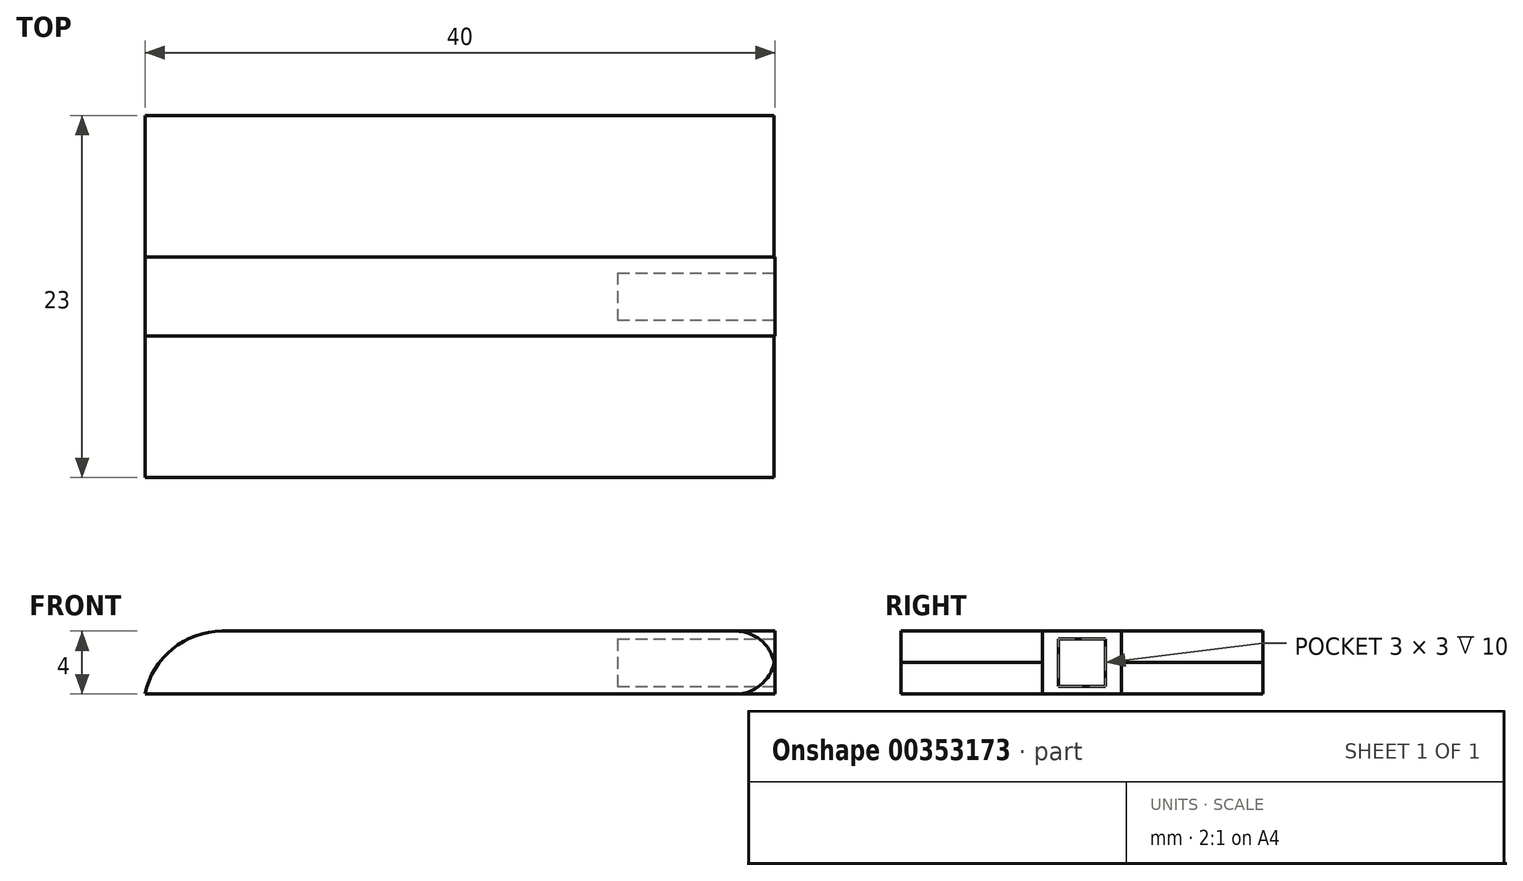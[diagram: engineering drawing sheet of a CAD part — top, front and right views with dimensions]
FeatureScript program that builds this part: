
annotation { "Feature Type Name" : "Feature", "Feature Type Description" : "" }
export const myFeature = defineFeature(function(context is Context, id is Id, definition is map)
    precondition{}
    {
        {
            var Q0;
            Q0=qCreatedBy(makeId("Right.planeOp"),FACE);
            var sketch = newSketch(context, id + "F0", { "sketchPlane" : qUnion([Q0])});
            skLineSegment(sketch, "E0.bottom", {"start": v(0, 0) * mm, "end": v(5, 0) * mm});
            skLineSegment(sketch, "E0.top", {"start": v(0, 4) * mm, "end": v(5, 4) * mm});
            skLineSegment(sketch, "E0.left", {"start": v(0, 0) * mm, "end": v(0, 4) * mm});
            skLineSegment(sketch, "E0.right", {"start": v(5, 0) * mm, "end": v(5, 4) * mm});
            skLineSegment(sketch, "E1.bottom", {"start": v(5, 4) * mm, "end": v(14, 4) * mm});
            skLineSegment(sketch, "E1.top", {"start": v(5, 0) * mm, "end": v(14, 0) * mm});
            skLineSegment(sketch, "E1.left", {"start": v(5, 4) * mm, "end": v(5, 0) * mm});
            skLineSegment(sketch, "E1.right", {"start": v(14, 4) * mm, "end": v(14, 0) * mm});
            skLineSegment(sketch, "E2.bottom", {"start": v(0, 4) * mm, "end": v(-9, 4) * mm});
            skLineSegment(sketch, "E2.top", {"start": v(0, 0) * mm, "end": v(-9, 0) * mm});
            skLineSegment(sketch, "E2.left", {"start": v(0, 4) * mm, "end": v(0, 0) * mm});
            skLineSegment(sketch, "E2.right", {"start": v(-9, 4) * mm, "end": v(-9, 0) * mm});
            skSolve(sketch);
        }
        {
            var Q0;
            Q0=makeQuery(id+"F0.imprint","IMPRINT",FACE,{"disambiguationData":[TD([[makeQuery(id+"F0.imprint","IMPRINT",EDGE,{"derivedFrom":sQuery(id+"F0.wireOp",EDGE,"E2.bottom")}),1.0]])]});
            var Q1;
            Q1=makeQuery(id+"F0.imprint","IMPRINT",FACE,{"disambiguationData":[TD([[makeQuery(id+"F0.imprint","IMPRINT",EDGE,{"derivedFrom":sQuery(id+"F0.wireOp",EDGE,"E1.bottom")}),-1.0]])]});
            extrude(context, id + "F1", {"entities" : qUnion([Q0, Q1]), "depth" : 40 * mm});
        }
        {
            var Q0;
            Q0=makeQuery(id+"F0.imprint","IMPRINT",FACE,{"disambiguationData":[TD([[makeQuery(id+"F0.imprint","IMPRINT",EDGE,{"derivedFrom":sQuery(id+"F0.wireOp",EDGE,"E0.bottom")}),1.0]])]});
            extrude(context, id + "F2", {"entities" : qUnion([Q0]), "depth" : 40 * mm});
        }
        {
            var Q0;
            Q0=makeQuery(id+"F2.opExtrude","CAP_FACE",FACE,{"disambiguationData":[OSD([sQuery(id+"F0.wireOp",EDGE,"E0.bottom"),sQuery(id+"F0.wireOp",EDGE,"E0.top"),sQuery(id+"F0.wireOp",EDGE,"E1.left"),sQuery(id+"F0.wireOp",EDGE,"E2.left")])],"isStart":false});
            var sketch = newSketch(context, id + "F3", { "sketchPlane" : qUnion([Q0])});
            skLineSegment(sketch, "E3", {"start": v(2.5, 4) * mm, "end": v(2.5, 0) * mm, "construction": true});
            skLineSegment(sketch, "E4", {"start": v(2.5, 0) * mm, "end": v(0, 2) * mm, "construction": true});
            skLineSegment(sketch, "E5", {"start": v(0, 2) * mm, "end": v(5, 2) * mm, "construction": true});
            skLineSegment(sketch, "E6.bottom", {"start": v(4, 3.5) * mm, "end": v(1, 3.5) * mm});
            skLineSegment(sketch, "E6.top", {"start": v(4, 0.5) * mm, "end": v(1, 0.5) * mm});
            skLineSegment(sketch, "E6.left", {"start": v(4, 3.5) * mm, "end": v(4, 0.5) * mm});
            skLineSegment(sketch, "E6.right", {"start": v(1, 3.5) * mm, "end": v(1, 0.5) * mm});
            skPoint(sketch, "E6.middle", {"position": v(2.5, 2) * mm});
            skSolve(sketch);
        }
        {
            var Q0;
            Q0=qSketchRegion(id+"F3",true);
            extrude(context, id + "F4", {"entities" : qUnion([Q0]), "operationType" : NewBodyOperationType.REMOVE, "oppositeDirection" : true, "depth" : 10 * mm});
        }
        {
            var Q0;
            Q0=makeQuery(id+"F1.opExtrude","CAP_EDGE",EDGE,{"disambiguationData":[OSD([sQuery(id+"F0.wireOp",EDGE,"E2.bottom")])],"isStart":true});
            var Q1;
            Q1=makeQuery(id+"F2.opExtrude","CAP_EDGE",EDGE,{"disambiguationData":[OSD([sQuery(id+"F0.wireOp",EDGE,"E0.top")])],"isStart":true});
            var Q2;
            Q2=makeQuery(id+"F1.opExtrude","CAP_EDGE",EDGE,{"disambiguationData":[OSD([sQuery(id+"F0.wireOp",EDGE,"E1.bottom")])],"isStart":true});
            fillet(context, id + "F5", {"entities" : qUnion([Q0, Q1, Q2]), "radius" : 5 * mm, "tangentPropagation" : true, "allowEdgeOverflow" : false});
        }
        {
            var Q0;
            Q0=makeQuery(id+"F1.opExtrude","CAP_EDGE",EDGE,{"disambiguationData":[OSD([sQuery(id+"F0.wireOp",EDGE,"E1.bottom")])],"isStart":false});
            var Q1;
            Q1=makeQuery(id+"F1.opExtrude","CAP_EDGE",EDGE,{"disambiguationData":[OSD([sQuery(id+"F0.wireOp",EDGE,"E1.top")])],"isStart":false});
            var Q2;
            Q2=makeQuery(id+"F1.opExtrude","CAP_EDGE",EDGE,{"disambiguationData":[OSD([sQuery(id+"F0.wireOp",EDGE,"E2.bottom")])],"isStart":false});
            var Q3;
            Q3=makeQuery(id+"F1.opExtrude","CAP_EDGE",EDGE,{"disambiguationData":[OSD([sQuery(id+"F0.wireOp",EDGE,"E2.top")])],"isStart":false});
            fillet(context, id + "F6", {"entities" : qUnion([Q0, Q1, Q2, Q3]), "radius" : 2.5 * mm, "tangentPropagation" : true, "allowEdgeOverflow" : false});
        }
    });
